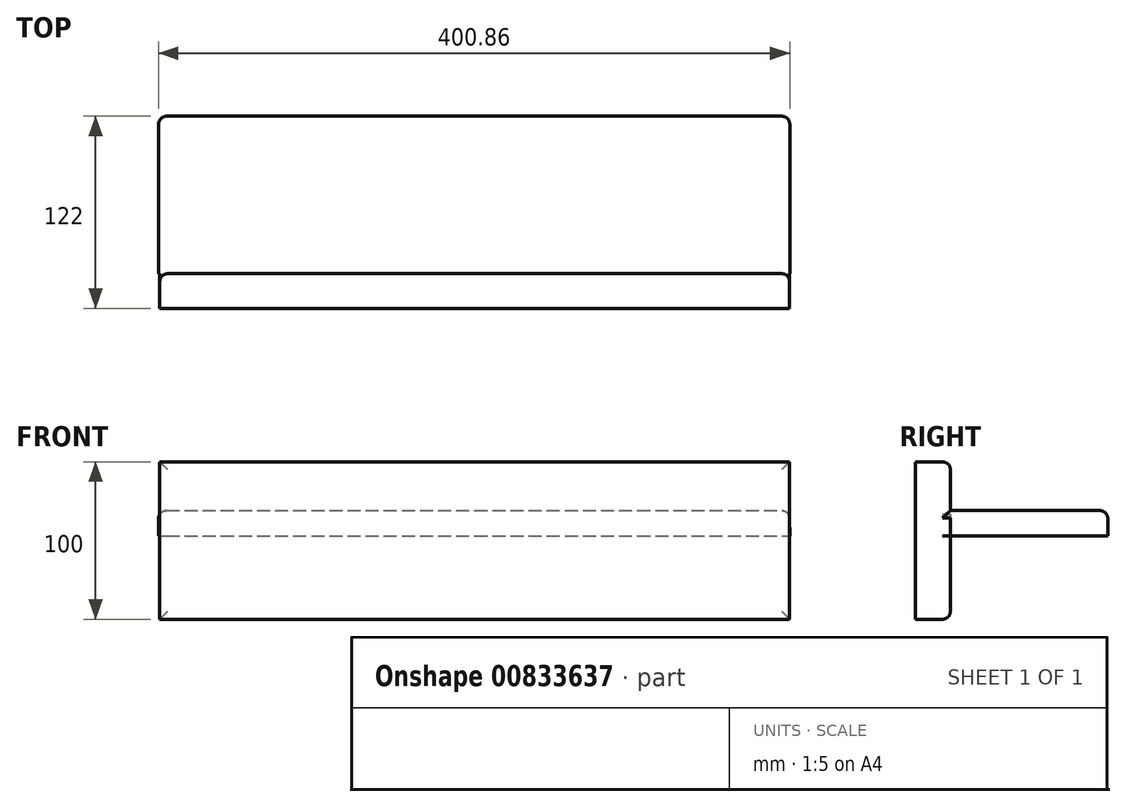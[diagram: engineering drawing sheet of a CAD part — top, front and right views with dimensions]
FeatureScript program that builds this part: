
annotation { "Feature Type Name" : "Feature", "Feature Type Description" : "" }
export const myFeature = defineFeature(function(context is Context, id is Id, definition is map)
    precondition{}
    {
        {
            var Q0;
            Q0=qCreatedBy(makeId("Front.planeOp"),FACE);
            var sketch = newSketch(context, id + "F0", { "sketchPlane" : qUnion([Q0])});
            skLineSegment(sketch, "E0.bottom", {"start": v(118.29, 41.72) * mm, "end": v(-281.71, 41.72) * mm});
            skLineSegment(sketch, "E0.top", {"start": v(118.29, -58.28) * mm, "end": v(-281.71, -58.28) * mm});
            skLineSegment(sketch, "E0.left", {"start": v(118.29, 41.72) * mm, "end": v(118.29, -58.28) * mm});
            skLineSegment(sketch, "E0.right", {"start": v(-281.71, 41.72) * mm, "end": v(-281.71, -58.28) * mm});
            skSolve(sketch);
        }
        {
            var Q0;
            Q0=qSketchRegion(id+"F0",true);
            extrude(context, id + "F1", {"entities" : qUnion([Q0]), "depth" : 22 * mm, "offsetDistance" : 25 * mm});
        }
        {
            var Q0;
            Q0=qCreatedBy(makeId("Front.planeOp"),FACE);
            var sketch = newSketch(context, id + "F2", { "sketchPlane" : qUnion([Q0])});
            skLineSegment(sketch, "E1", {"start": v(-282.49, 10.71) * mm, "end": v(118.3, 10.71) * mm});
            skLineSegment(sketch, "E2", {"start": v(-282.49, 10.71) * mm, "end": v(-282.49, -5.47) * mm});
            skLineSegment(sketch, "E3", {"start": v(-282.49, -5.47) * mm, "end": v(118.37, -5.47) * mm});
            skLineSegment(sketch, "E4", {"start": v(118.3, 10.71) * mm, "end": v(118.37, -5.47) * mm});
            skSolve(sketch);
        }
        {
            var Q0;
            Q0=qSketchRegion(id+"F2",true);
            extrude(context, id + "F3", {"entities" : qUnion([Q0]), "operationType" : NewBodyOperationType.ADD, "depth" : -100 * mm, "offsetDistance" : 25 * mm});
        }
        {
            var Q0;
            Q0=makeQuery(id+"F3.opExtrude","SWEPT_EDGE",EDGE,{"disambiguationData":[OSD([sQuery(id+"F2.wireOp",EDGE,"E1"),sQuery(id+"F2.wireOp",EDGE,"E4")])]});
            var Q1;
            Q1=makeQuery(id+"F3.opExtrude","CAP_EDGE",EDGE,{"disambiguationData":[OSD([sQuery(id+"F2.wireOp",EDGE,"E1")])],"isStart":false});
            var Q2;
            Q2=makeQuery(id+"F3.opExtrude","SWEPT_EDGE",EDGE,{"disambiguationData":[OSD([sQuery(id+"F2.wireOp",EDGE,"E1"),sQuery(id+"F2.wireOp",EDGE,"E2")])]});
            fillet(context, id + "F4", {"entities" : qUnion([Q0, Q1, Q2]), "radius" : 5 * mm, "tangentPropagation" : true, "allowEdgeOverflow" : false});
        }
        {
            var Q0;
            Q0=makeQuery(id+"F1.opExtrude","CAP_EDGE",EDGE,{"disambiguationData":[OSD([sQuery(id+"F0.wireOp",EDGE,"E0.bottom")])],"isStart":true});
            var Q1;
            {var subQ0=sQuery(id+"F0.wireOp",EDGE,"E0.left");var subQ1=makeQuery(id+"F1.opExtrude","SWEPT_FACE",FACE,{"disambiguationData":[OSD([subQ0])]});var subQ2=sQuery(id+"F2.wireOp",EDGE,"E4");var subQ3=sQuery(id+"F2.wireOp",EDGE,"E1");var subQ4=makeQuery(id+"F3.opExtrude","CAP_FACE",FACE,{"disambiguationData":[OSD([subQ3,sQuery(id+"F2.wireOp",EDGE,"E2"),sQuery(id+"F2.wireOp",EDGE,"E3"),subQ2])],"isStart":true});var subQ5=makeQuery(id+"F1.opExtrude","CAP_EDGE",EDGE,{"disambiguationData":[OSD([subQ0])],"isStart":true});var subQ6=sQuery(id+"F0.wireOp",EDGE,"E0.bottom");var subQ7=makeQuery(id+"F1.opExtrude","CAP_FACE",FACE,{"disambiguationData":[OSD([subQ6,sQuery(id+"F0.wireOp",EDGE,"E0.top"),subQ0,sQuery(id+"F0.wireOp",EDGE,"E0.right")])],"isStart":true});Q1=makeQuery(id+"F4.opFillet","MERGE",EDGE,{"derivedFrom":[makeQuery(id+"F3.boolean.opBoolean","SPLIT",EDGE,{"disambiguationData":[topologyDisambiguationEdgeConnected([subQ7,subQ1]),TD([makeQuery(id+"F1.opExtrude","SWEPT_FACE",FACE,{"disambiguationData":[OSD([subQ6])]})])],"derivedFrom":subQ5}),makeQuery(id+"F3.boolean.opBoolean","SPLIT",EDGE,{"disambiguationData":[topologyDisambiguationEdgeConnected([subQ1,subQ4])],"derivedFrom":subQ5})]});}
            var Q2;
            Q2=makeQuery(id+"F1.opExtrude","CAP_EDGE",EDGE,{"disambiguationData":[OSD([sQuery(id+"F0.wireOp",EDGE,"E0.top")])],"isStart":true});
            var Q3;
            {var subQ1=sQuery(id+"F0.wireOp",EDGE,"E0.right");var subQ2=makeQuery(id+"F1.opExtrude","SWEPT_FACE",FACE,{"disambiguationData":[OSD([subQ1])]});var subQ3=sQuery(id+"F0.wireOp",EDGE,"E0.top");var subQ4=makeQuery(id+"F1.opExtrude","CAP_FACE",FACE,{"disambiguationData":[OSD([sQuery(id+"F0.wireOp",EDGE,"E0.bottom"),subQ3,sQuery(id+"F0.wireOp",EDGE,"E0.left"),subQ1])],"isStart":true});Q3=makeQuery(id+"F3.boolean.opBoolean","SPLIT",EDGE,{"disambiguationData":[topologyDisambiguationEdgeConnected([subQ4,subQ2]),TD([makeQuery(id+"F1.opExtrude","SWEPT_FACE",FACE,{"disambiguationData":[OSD([subQ3])]})])],"derivedFrom":makeQuery(id+"F1.opExtrude","CAP_EDGE",EDGE,{"disambiguationData":[OSD([subQ1])],"isStart":true})});}
            var Q4;
            {var subQ0=sQuery(id+"F0.wireOp",EDGE,"E0.right");var subQ1=makeQuery(id+"F1.opExtrude","SWEPT_FACE",FACE,{"disambiguationData":[OSD([subQ0])]});var subQ2=sQuery(id+"F2.wireOp",EDGE,"E1");var subQ3=makeQuery(id+"F3.opExtrude","CAP_FACE",FACE,{"disambiguationData":[OSD([subQ2,sQuery(id+"F2.wireOp",EDGE,"E2"),sQuery(id+"F2.wireOp",EDGE,"E3"),sQuery(id+"F2.wireOp",EDGE,"E4")])],"isStart":true});var subQ4=makeQuery(id+"F1.opExtrude","CAP_EDGE",EDGE,{"disambiguationData":[OSD([subQ0])],"isStart":true});var subQ5=sQuery(id+"F0.wireOp",EDGE,"E0.bottom");var subQ6=makeQuery(id+"F1.opExtrude","CAP_FACE",FACE,{"disambiguationData":[OSD([subQ5,sQuery(id+"F0.wireOp",EDGE,"E0.top"),sQuery(id+"F0.wireOp",EDGE,"E0.left"),subQ0])],"isStart":true});Q4=makeQuery(id+"F4.opFillet","MERGE",EDGE,{"derivedFrom":[makeQuery(id+"F3.boolean.opBoolean","SPLIT",EDGE,{"disambiguationData":[topologyDisambiguationEdgeConnected([subQ6,subQ1]),TD([makeQuery(id+"F1.opExtrude","SWEPT_FACE",FACE,{"disambiguationData":[OSD([subQ5])]})])],"derivedFrom":subQ4}),makeQuery(id+"F3.boolean.opBoolean","SPLIT",EDGE,{"disambiguationData":[topologyDisambiguationEdgeConnected([subQ1,subQ3])],"derivedFrom":subQ4})]});}
            var Q5;
            {var subQ1=sQuery(id+"F0.wireOp",EDGE,"E0.left");var subQ2=makeQuery(id+"F1.opExtrude","SWEPT_FACE",FACE,{"disambiguationData":[OSD([subQ1])]});var subQ3=sQuery(id+"F0.wireOp",EDGE,"E0.top");var subQ4=makeQuery(id+"F1.opExtrude","CAP_FACE",FACE,{"disambiguationData":[OSD([sQuery(id+"F0.wireOp",EDGE,"E0.bottom"),subQ3,subQ1,sQuery(id+"F0.wireOp",EDGE,"E0.right")])],"isStart":true});Q5=makeQuery(id+"F3.boolean.opBoolean","SPLIT",EDGE,{"disambiguationData":[topologyDisambiguationEdgeConnected([subQ4,subQ2]),TD([makeQuery(id+"F1.opExtrude","SWEPT_FACE",FACE,{"disambiguationData":[OSD([subQ3])]})])],"derivedFrom":makeQuery(id+"F1.opExtrude","CAP_EDGE",EDGE,{"disambiguationData":[OSD([subQ1])],"isStart":true})});}
            fillet(context, id + "F5", {"entities" : qUnion([Q0, Q1, Q2, Q3, Q4, Q5]), "radius" : 5 * mm, "tangentPropagation" : true, "allowEdgeOverflow" : false});
        }
        {
            var Q0;
            Q0=makeQuery(id+"F3.opExtrude","CAP_EDGE",EDGE,{"disambiguationData":[OSD([sQuery(id+"F2.wireOp",EDGE,"E2")])],"isStart":false});
            var Q1;
            Q1=makeQuery(id+"F3.opExtrude","CAP_EDGE",EDGE,{"disambiguationData":[OSD([sQuery(id+"F2.wireOp",EDGE,"E4")])],"isStart":false});
            fillet(context, id + "F6", {"entities" : qUnion([Q0, Q1]), "radius" : 5 * mm, "tangentPropagation" : true, "allowEdgeOverflow" : false});
        }
    });
